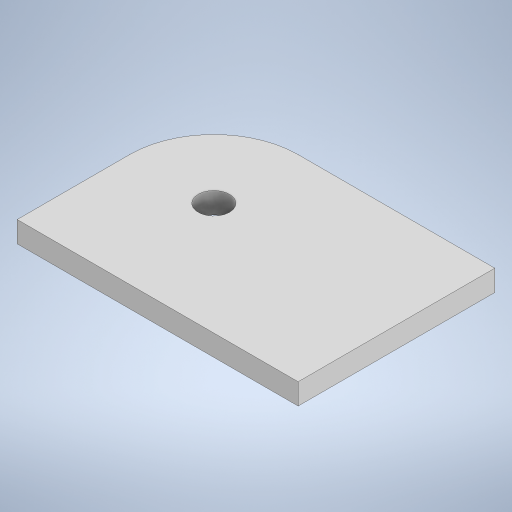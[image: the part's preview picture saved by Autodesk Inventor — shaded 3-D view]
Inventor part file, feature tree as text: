
AUTODESK INVENTOR PART (.ipt)
format: ipt  version: 2024 (Build 280153000, 153)  size: 211,968 bytes
history: native  units: mm
features: extrude x2, sketch x2, fillet x1
ambient origin geometry x8: Origin, YZ Plane, XZ Plane, XY Plane, X Axis, Y Axis, Z Axis, Center Point
bodies: Solid1 (feature_tree)
feature tree (5):
  extrude  "Extrusion1"  Depth=200.0mm
  fillet  "Fillet2"  Radius=15.0mm
  extrude  "Extrusion2"  Depth=15.0mm TaperAngle=0.0deg
  sketch  "Sketch1"  dims[d0=140.0mm d1=200.0mm d2=15.0mm d3=0.0mm]
  sketch  "Sketch2"  dims[d5=60.0mm d6=15.0mm d7=0.0mm]
